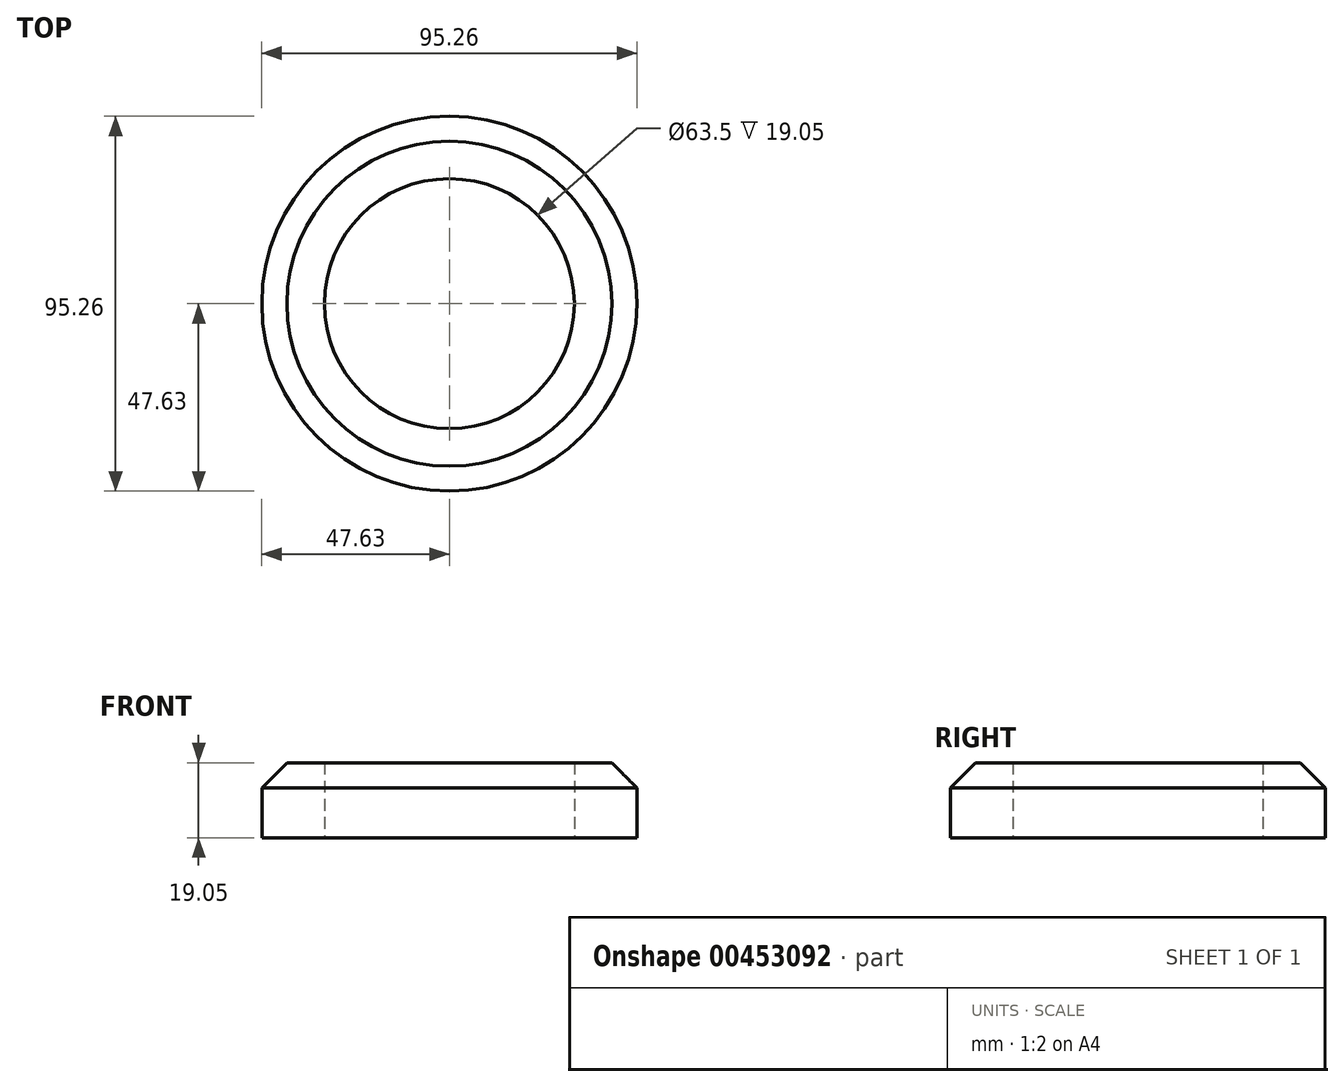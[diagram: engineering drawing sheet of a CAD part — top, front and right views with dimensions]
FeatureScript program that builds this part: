
annotation { "Feature Type Name" : "Feature", "Feature Type Description" : "" }
export const myFeature = defineFeature(function(context is Context, id is Id, definition is map)
    precondition{}
    {
        {
            var Q0;
            Q0=qCreatedBy(makeId("Top.planeOp"),FACE);
            var sketch = newSketch(context, id + "F0", { "sketchPlane" : qUnion([Q0])});
            skCircle(sketch, "E0", {"center": v(0, 0) * mm, "radius": 31.75 * mm});
            skCircle(sketch, "E1", {"center": v(0, 0) * mm, "radius": 47.63 * mm});
            skSolve(sketch);
        }
        {
            var Q0;
            Q0 = qSketchRegion(id + "F0", true);
            extrude(context, id + "F1", {"entities" : qUnion([Q0]), "depth" : 19.05 * mm, "offsetDistance" : 25.4 * mm});
        }
        {
            var Q0;
            Q0=makeQuery(id+"F1.opExtrude","CAP_EDGE",EDGE,{"disambiguationData":[OSD([sQuery(id+"F0.wireOp",EDGE,"E1")])],"isStart":false});
            chamfer(context, id + "F2", {"entities" : qUnion([Q0]), "width" : 6.35 * mm, "tangentPropagation" : true});
        }
    });
